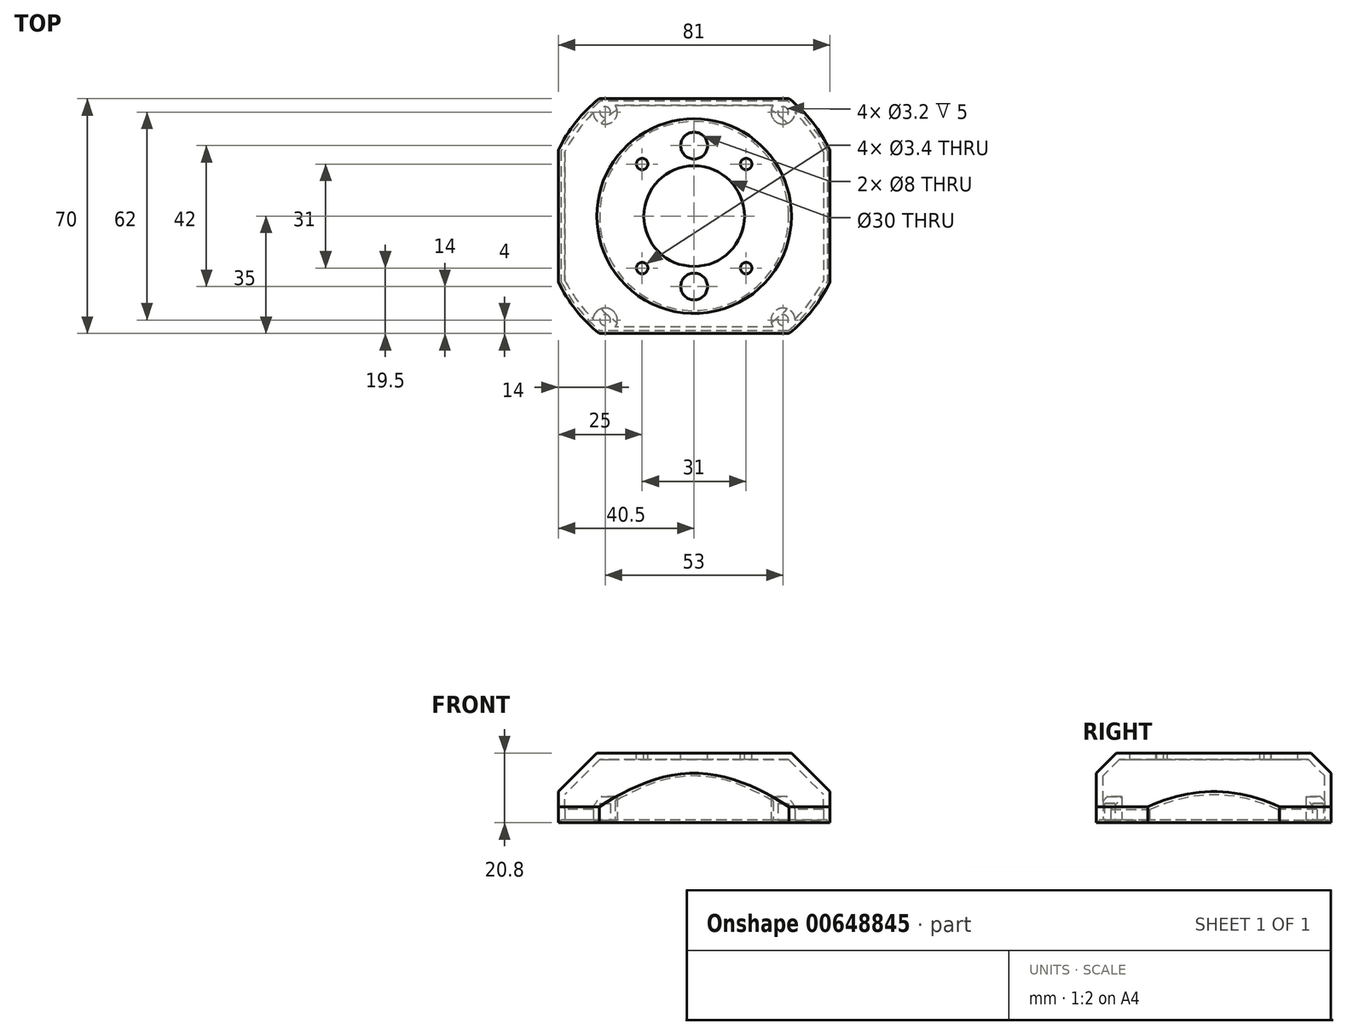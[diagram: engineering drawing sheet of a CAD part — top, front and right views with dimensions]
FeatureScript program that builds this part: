
annotation { "Feature Type Name" : "Feature", "Feature Type Description" : "" }
export const myFeature = defineFeature(function(context is Context, id is Id, definition is map)
    precondition{}
    {
        {
            var Q0;
            Q0=qCreatedBy(makeId("Top.planeOp"),FACE);
            var sketch = newSketch(context, id + "F0", { "sketchPlane" : qUnion([Q0])});
            skLineSegment(sketch, "E0.bottom", {"start": v(28.28, 35) * mm, "end": v(-28.28, 35) * mm});
            skLineSegment(sketch, "E0.top", {"start": v(28.28, -35) * mm, "end": v(-28.28, -35) * mm});
            skLineSegment(sketch, "E0.left", {"start": v(40.5, 19.62) * mm, "end": v(40.5, -19.62) * mm});
            skLineSegment(sketch, "E0.right", {"start": v(-40.5, 19.62) * mm, "end": v(-40.5, -19.62) * mm});
            skPoint(sketch, "E0.middle", {"position": v(0, 0) * mm});
            skArc(sketch, "E1", {"start": v(-28.28, 35) * mm, "mid": v(-35.24, 27.98) * mm, "end": v(-40.5, 19.62) * mm});
            skPoint(sketch, "E2.orphan", {"position": v(-40.5, 35) * mm});
            skArc(sketch, "E3.trimOffspring", {"start": v(-40.5, -19.62) * mm, "mid": v(-35.24, -27.98) * mm, "end": v(-28.28, -35) * mm});
            skPoint(sketch, "E4.orphan", {"position": v(-40.5, -35) * mm});
            skArc(sketch, "E5.trimOffspring", {"start": v(28.28, -35) * mm, "mid": v(35.24, -27.98) * mm, "end": v(40.5, -19.62) * mm});
            skPoint(sketch, "E6.orphan", {"position": v(40.5, -35) * mm});
            skArc(sketch, "E7.trimOffspring", {"start": v(40.5, 19.62) * mm, "mid": v(35.24, 27.98) * mm, "end": v(28.28, 35) * mm});
            skPoint(sketch, "E8.orphan", {"position": v(40.5, 35) * mm});
            skSolve(sketch);
        }
        {
            var Q0;
            Q0=makeQuery(id+"F0.imprint","IMPRINT",FACE,{"disambiguationData":[TD([[makeQuery(id+"F0.imprint","IMPRINT",EDGE,{"derivedFrom":sQuery(id+"F0.wireOp",EDGE,"E0.bottom")}),1.0]])]});
            extrude(context, id + "F1", {"entities" : qUnion([Q0]), "depth" : 20 * mm, "offsetDistance" : 25 * mm});
        }
        {
            var Q0;
            Q0=makeQuery(id+"F1.opExtrude","CAP_EDGE",EDGE,{"disambiguationData":[OSD([sQuery(id+"F0.wireOp",EDGE,"E1")])],"isStart":false});
            var Q1;
            Q1=makeQuery(id+"F1.opExtrude","CAP_EDGE",EDGE,{"disambiguationData":[OSD([sQuery(id+"F0.wireOp",EDGE,"E3.trimOffspring")])],"isStart":false});
            var Q2;
            Q2=makeQuery(id+"F1.opExtrude","CAP_EDGE",EDGE,{"disambiguationData":[OSD([sQuery(id+"F0.wireOp",EDGE,"E5.trimOffspring")])],"isStart":false});
            var Q3;
            Q3=makeQuery(id+"F1.opExtrude","CAP_EDGE",EDGE,{"disambiguationData":[OSD([sQuery(id+"F0.wireOp",EDGE,"E7.trimOffspring")])],"isStart":false});
            chamfer(context, id + "F2", {"entities" : qUnion([Q0, Q1, Q2, Q3]), "width" : 16 * mm, "tangentPropagation" : true});
        }
        {
            var Q0;
            Q0=makeQuery(id+"F1.opExtrude","CAP_FACE",FACE,{"disambiguationData":[OSD([sQuery(id+"F0.wireOp",EDGE,"E0.bottom"),sQuery(id+"F0.wireOp",EDGE,"E0.top"),sQuery(id+"F0.wireOp",EDGE,"E0.left"),sQuery(id+"F0.wireOp",EDGE,"E0.right"),sQuery(id+"F0.wireOp",EDGE,"E1"),sQuery(id+"F0.wireOp",EDGE,"E3.trimOffspring"),sQuery(id+"F0.wireOp",EDGE,"E5.trimOffspring"),sQuery(id+"F0.wireOp",EDGE,"E7.trimOffspring")])],"isStart":true});
            var sketch = newSketch(context, id + "F3", { "sketchPlane" : qUnion([Q0])});
            skCircle(sketch, "E9", {"center": v(-26.5, 31) * mm, "radius": 1.6 * mm});
            skCircle(sketch, "E10", {"center": v(26.5, 31) * mm, "radius": 1.6 * mm});
            skCircle(sketch, "E11", {"center": v(26.5, -31) * mm, "radius": 1.6 * mm});
            skCircle(sketch, "E12", {"center": v(-26.5, -31) * mm, "radius": 1.6 * mm});
            skSolve(sketch);
        }
        {
            var Q0;
            Q0=makeQuery(id+"F3.imprint","IMPRINT",FACE,{"disambiguationData":[TD([[makeQuery(id+"F3.imprint","IMPRINT",EDGE,{"derivedFrom":sQuery(id+"F3.wireOp",EDGE,"E9")}),1.0]])]});
            var Q1;
            Q1=makeQuery(id+"F3.imprint","IMPRINT",FACE,{"disambiguationData":[TD([[makeQuery(id+"F3.imprint","IMPRINT",EDGE,{"derivedFrom":sQuery(id+"F3.wireOp",EDGE,"E11")}),1.0]])]});
            var Q2;
            Q2=makeQuery(id+"F3.imprint","IMPRINT",FACE,{"disambiguationData":[TD([[makeQuery(id+"F3.imprint","IMPRINT",EDGE,{"derivedFrom":sQuery(id+"F3.wireOp",EDGE,"E12")}),1.0]])]});
            var Q3;
            Q3=makeQuery(id+"F3.imprint","IMPRINT",FACE,{"disambiguationData":[TD([[makeQuery(id+"F3.imprint","IMPRINT",EDGE,{"derivedFrom":sQuery(id+"F3.wireOp",EDGE,"E10")}),1.0]])]});
            extrude(context, id + "F4", {"entities" : qUnion([Q0, Q1, Q2, Q3]), "operationType" : NewBodyOperationType.REMOVE, "oppositeDirection" : true, "depth" : 5 * mm, "offsetDistance" : 25 * mm});
        }
        {
            var Q0;
            Q0=makeQuery(id+"F1.opExtrude","CAP_FACE",FACE,{"disambiguationData":[OSD([sQuery(id+"F0.wireOp",EDGE,"E0.bottom"),sQuery(id+"F0.wireOp",EDGE,"E0.top"),sQuery(id+"F0.wireOp",EDGE,"E0.left"),sQuery(id+"F0.wireOp",EDGE,"E0.right"),sQuery(id+"F0.wireOp",EDGE,"E1"),sQuery(id+"F0.wireOp",EDGE,"E3.trimOffspring"),sQuery(id+"F0.wireOp",EDGE,"E5.trimOffspring"),sQuery(id+"F0.wireOp",EDGE,"E7.trimOffspring")])],"isStart":true});
            shell(context, id + "F5", {"entities" : qUnion([Q0]), "thickness" : 2 * mm});
        }
        {
            var Q0;
            Q0=makeQuery(id+"F1.opExtrude","CAP_FACE",FACE,{"disambiguationData":[OSD([sQuery(id+"F0.wireOp",EDGE,"E0.bottom"),sQuery(id+"F0.wireOp",EDGE,"E0.top"),sQuery(id+"F0.wireOp",EDGE,"E0.left"),sQuery(id+"F0.wireOp",EDGE,"E0.right"),sQuery(id+"F0.wireOp",EDGE,"E1"),sQuery(id+"F0.wireOp",EDGE,"E3.trimOffspring"),sQuery(id+"F0.wireOp",EDGE,"E5.trimOffspring"),sQuery(id+"F0.wireOp",EDGE,"E7.trimOffspring")])],"isStart":true});
            var sketch = newSketch(context, id + "F6", { "sketchPlane" : qUnion([Q0])});
            skLineSegment(sketch, "E13.0", {"start": v(28, 34.2) * mm, "end": v(-28, 34.2) * mm});
            skArc(sketch, "E13.1", {"start": v(-39.7, 19.43) * mm, "mid": v(-34.65, 27.45) * mm, "end": v(-28, 34.2) * mm});
            skArc(sketch, "E13.2", {"start": v(28, 34.2) * mm, "mid": v(34.65, 27.45) * mm, "end": v(39.7, 19.43) * mm});
            skLineSegment(sketch, "E13.3", {"start": v(-39.7, -19.43) * mm, "end": v(-39.7, 19.43) * mm});
            skLineSegment(sketch, "E13.4", {"start": v(39.7, -19.43) * mm, "end": v(39.7, 19.43) * mm});
            skArc(sketch, "E13.5", {"start": v(39.7, -19.43) * mm, "mid": v(34.65, -27.45) * mm, "end": v(28, -34.2) * mm});
            skLineSegment(sketch, "E13.6", {"start": v(28, -34.2) * mm, "end": v(-28, -34.2) * mm});
            skArc(sketch, "E13.7", {"start": v(-28, -34.2) * mm, "mid": v(-34.65, -27.45) * mm, "end": v(-39.7, -19.43) * mm});
            skSolve(sketch);
        }
        {
            var Q0;
            Q0=makeQuery(id+"F6.imprint","IMPRINT",FACE,{"disambiguationData":[TD([[makeQuery(id+"F6.imprint","IMPRINT",EDGE,{"derivedFrom":sQuery(id+"F6.wireOp",EDGE,"E13.0")}),-1.0]])]});
            extrude(context, id + "F7", {"entities" : qUnion([Q0]), "operationType" : NewBodyOperationType.ADD, "depth" : 0.8 * mm, "offsetDistance" : 25 * mm});
        }
        {
            var Q0;
            Q0=makeQuery(id+"F1.opExtrude","CAP_FACE",FACE,{"disambiguationData":[OSD([sQuery(id+"F0.wireOp",EDGE,"E0.bottom"),sQuery(id+"F0.wireOp",EDGE,"E0.top"),sQuery(id+"F0.wireOp",EDGE,"E0.left"),sQuery(id+"F0.wireOp",EDGE,"E0.right"),sQuery(id+"F0.wireOp",EDGE,"E1"),sQuery(id+"F0.wireOp",EDGE,"E3.trimOffspring"),sQuery(id+"F0.wireOp",EDGE,"E5.trimOffspring"),sQuery(id+"F0.wireOp",EDGE,"E7.trimOffspring")])],"isStart":false});
            var sketch = newSketch(context, id + "F8", { "sketchPlane" : qUnion([Q0])});
            skCircle(sketch, "E14", {"center": v(0, 0) * mm, "radius": 15 * mm});
            skLineSegment(sketch, "E15.bottom", {"start": v(15.5, 15.5) * mm, "end": v(-15.5, 15.5) * mm, "construction": true});
            skLineSegment(sketch, "E15.top", {"start": v(15.5, -15.5) * mm, "end": v(-15.5, -15.5) * mm, "construction": true});
            skLineSegment(sketch, "E15.left", {"start": v(15.5, 15.5) * mm, "end": v(15.5, -15.5) * mm, "construction": true});
            skLineSegment(sketch, "E15.right", {"start": v(-15.5, 15.5) * mm, "end": v(-15.5, -15.5) * mm, "construction": true});
            skCircle(sketch, "E16", {"center": v(-15.5, 15.5) * mm, "radius": 1.7 * mm});
            skCircle(sketch, "E17", {"center": v(15.5, 15.5) * mm, "radius": 1.7 * mm});
            skCircle(sketch, "E18", {"center": v(15.5, -15.5) * mm, "radius": 1.7 * mm});
            skCircle(sketch, "E19", {"center": v(-15.5, -15.5) * mm, "radius": 1.7 * mm});
            skCircle(sketch, "E20", {"center": v(0, 21) * mm, "radius": 4 * mm});
            skCircle(sketch, "E21", {"center": v(0, -21) * mm, "radius": 4 * mm});
            skSolve(sketch);
        }
        {
            var Q0;
            Q0 = qSketchRegion(id + "F8", true);
            extrude(context, id + "F9", {"entities" : qUnion([Q0]), "operationType" : NewBodyOperationType.REMOVE, "endBound" : BoundingType.THROUGH_ALL, "oppositeDirection" : true, "depth" : 25 * mm, "offsetDistance" : 25 * mm});
        }
    });
